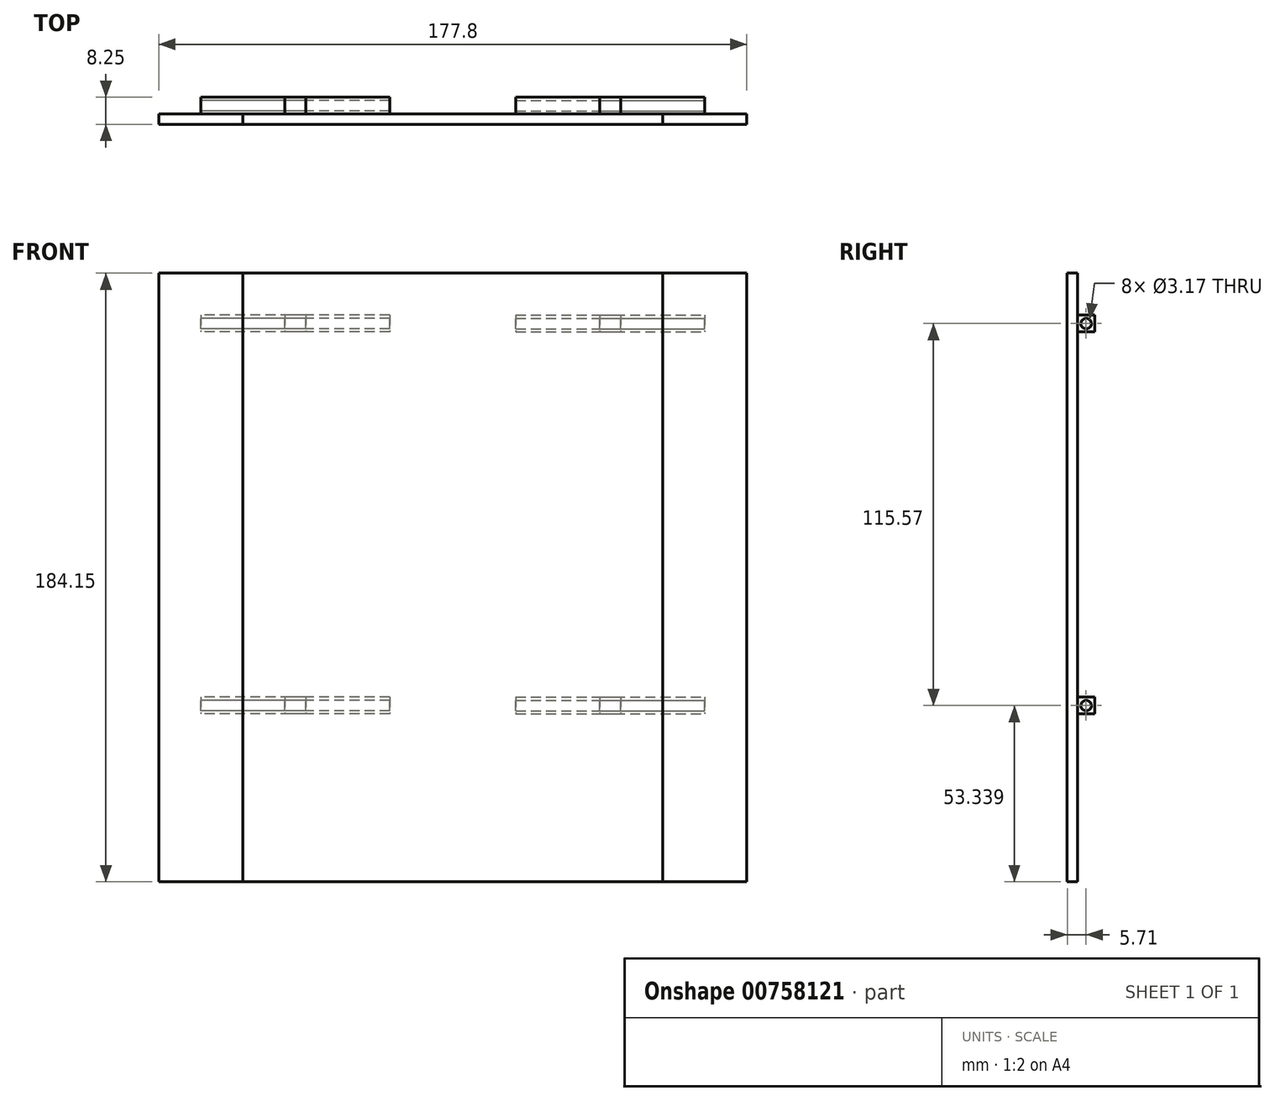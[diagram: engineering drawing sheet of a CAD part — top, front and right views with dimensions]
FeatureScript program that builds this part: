
annotation { "Feature Type Name" : "Feature", "Feature Type Description" : "" }
export const myFeature = defineFeature(function(context is Context, id is Id, definition is map)
    precondition{}
    {
        {
            var Q0;
            Q0=qCreatedBy(makeId("Front.planeOp"),FACE);
            var sketch = newSketch(context, id + "F0", { "sketchPlane" : qUnion([Q0])});
            skLineSegment(sketch, "E0", {"start": v(174.9, 31.47) * mm, "end": v(174.9, -152.68) * mm});
            skLineSegment(sketch, "E1", {"start": v(22.5, -152.68) * mm, "end": v(174.9, -152.68) * mm});
            skLineSegment(sketch, "E2", {"start": v(72.2, -149.5) * mm, "end": v(72.2, -81.5) * mm});
            skLineSegment(sketch, "E3", {"start": v(125.2, -81.5) * mm, "end": v(125.2, -149.5) * mm});
            skPoint(sketch, "E4.end.orphan", {"position": v(22.5, 4.94) * mm});
            skLineSegment(sketch, "E5", {"start": v(22.5, 31.47) * mm, "end": v(22.5, -152.68) * mm});
            skLineSegment(sketch, "E6", {"start": v(22.5, 31.47) * mm, "end": v(174.9, 31.47) * mm});
            skLineSegment(sketch, "E7", {"start": v(98.7, 31.47) * mm, "end": v(98.7, -152.68) * mm});
            skLineSegment(sketch, "E8", {"start": v(125.2, -81.5) * mm, "end": v(125.2, -81.5) * mm});
            skLineSegment(sketch, "E9", {"start": v(125.2, -81.5) * mm, "end": v(72.2, -81.5) * mm});
            skLineSegment(sketch, "E10", {"start": v(72.2, -81.5) * mm, "end": v(72.2, -81.5) * mm});
            skLineSegment(sketch, "E11", {"start": v(125.2, -149.5) * mm, "end": v(72.2, -149.5) * mm});
            skPoint(sketch, "E12", {"position": v(125.2, -149.5) * mm});
            skLineSegment(sketch, "E13.bottom", {"start": v(128.38, -78.33) * mm, "end": v(69.03, -78.33) * mm});
            skLineSegment(sketch, "E13.top", {"start": v(128.38, -152.68) * mm, "end": v(69.03, -152.68) * mm});
            skLineSegment(sketch, "E13.left", {"start": v(128.38, -78.33) * mm, "end": v(128.38, -152.68) * mm});
            skLineSegment(sketch, "E13.right", {"start": v(69.03, -78.33) * mm, "end": v(69.03, -152.68) * mm});
            skLineSegment(sketch, "E14", {"start": v(128.38, -115.5) * mm, "end": v(125.2, -115.5) * mm, "construction": true});
            skLineSegment(sketch, "E15", {"start": v(72.2, -115.5) * mm, "end": v(69.03, -115.5) * mm, "construction": true});
            skLineSegment(sketch, "E16", {"start": v(196.95, -166.3) * mm, "end": v(-6.25, -166.3) * mm, "construction": true});
            skLineSegment(sketch, "E17", {"start": v(-6.25, -166.3) * mm, "end": v(-6.25, 36.9) * mm, "construction": true});
            skLineSegment(sketch, "E18", {"start": v(-6.25, 36.9) * mm, "end": v(196.95, 36.9) * mm, "construction": true});
            skLineSegment(sketch, "E19", {"start": v(196.95, 36.9) * mm, "end": v(196.95, -166.3) * mm, "construction": true});
            skSolve(sketch);
        }
        {
            var Q0;
            {var subQ0=sQuery(id+"F0.wireOp",EDGE,"E3");Q0=makeQuery(id+"F0.imprint","IMPRINT",FACE,{"disambiguationData":[TD([[makeQuery(id+"F0.imprint","IMPRINT",EDGE,{"derivedFrom":subQ0}),1.0]])]});}
            var Q1;
            {var subQ3=sQuery(id+"F0.wireOp",EDGE,"ysnHI75o-22RJ-AJUc-xlc0-5ASTMfBeKelk");Q1=makeQuery(id+"F0.imprint","IMPRINT",FACE,{"disambiguationData":[TD([[makeQuery(id+"F0.imprint","IMPRINT",EDGE,{"derivedFrom":subQ3}),1.0]])]});}
            var Q2;
            {var subQ5=sQuery(id+"F0.wireOp",EDGE,"E0");Q2=makeQuery(id+"F0.imprint","IMPRINT",FACE,{"disambiguationData":[TD([[makeQuery(id+"F0.imprint","IMPRINT",EDGE,{"derivedFrom":subQ5}),-1.0]])]});}
            var Q3;
            {var subQ0=sQuery(id+"F0.wireOp",EDGE,"E3");Q3=makeQuery(id+"F0.imprint","IMPRINT",FACE,{"disambiguationData":[TD([[makeQuery(id+"F0.imprint","IMPRINT",EDGE,{"derivedFrom":subQ0}),-1.0]])]});}
            extrude(context, id + "F1", {"entities" : qUnion([Q0, Q1, Q2, Q3]), "depth" : 3.17 * mm, "offsetDistance" : 25.4 * mm});
        }
        {
            var Q0;
            Q0=makeQuery(id+"F1.opExtrude","SWEPT_FACE",FACE,{"disambiguationData":[OSD([sQuery(id+"F0.wireOp",EDGE,"E0")])]});
            var sketch = newSketch(context, id + "F2", { "sketchPlane" : qUnion([Q0])});
            skLineSegment(sketch, "E20.bottom", {"start": v(0, 18.77) * mm, "end": v(5.08, 18.77) * mm});
            skLineSegment(sketch, "E20.top", {"start": v(0, 13.69) * mm, "end": v(5.08, 13.69) * mm});
            skLineSegment(sketch, "E20.left", {"start": v(0, 18.77) * mm, "end": v(0, 13.69) * mm});
            skLineSegment(sketch, "E20.right", {"start": v(5.08, 18.77) * mm, "end": v(5.08, 13.69) * mm});
            skLineSegment(sketch, "E21.bottom", {"start": v(0, -96.8) * mm, "end": v(5.08, -96.8) * mm});
            skLineSegment(sketch, "E21.top", {"start": v(0, -101.88) * mm, "end": v(5.08, -101.88) * mm});
            skLineSegment(sketch, "E21.left", {"start": v(0, -96.8) * mm, "end": v(0, -101.88) * mm});
            skLineSegment(sketch, "E21.right", {"start": v(5.08, -96.8) * mm, "end": v(5.08, -101.88) * mm});
            skLineSegment(sketch, "E22", {"start": v(2.54, -101.88) * mm, "end": v(2.54, -96.8) * mm, "construction": true});
            skPoint(sketch, "E23", {"position": v(2.54, -99.34) * mm});
            skLineSegment(sketch, "E24", {"start": v(2.54, 18.77) * mm, "end": v(2.54, 13.69) * mm, "construction": true});
            skPoint(sketch, "E25", {"position": v(2.54, 16.23) * mm});
            skCircle(sketch, "E26", {"center": v(2.54, 16.23) * mm, "radius": 1.59 * mm});
            skCircle(sketch, "E27", {"center": v(2.54, -99.34) * mm, "radius": 1.59 * mm});
            skSolve(sketch);
        }
        {
            var Q0;
            Q0 = qSketchRegion(id + "F2", true);
            extrude(context, id + "F3", {"entities" : qUnion([Q0]), "operationType" : NewBodyOperationType.ADD, "oppositeDirection" : true, "depth" : 44.45 * mm, "offsetDistance" : 25.4 * mm, "hasSecondDirection" : true, "secondDirectionOppositeDirection" : true, "secondDirectionDepth" : 12.7 * mm});
        }
        {
            var Q0;
            Q0=makeQuery(id+"F1.opExtrude","SWEPT_BODY",BODY,{"disambiguationData":[OSD([sQuery(id+"F0.wireOp",EDGE,"E0"),sQuery(id+"F0.wireOp",EDGE,"E1"),sQuery(id+"F0.wireOp",EDGE,"E6"),sQuery(id+"F0.wireOp",EDGE,"E7"),sQuery(id+"F0.wireOp",EDGE,"E13.top")])]});
            var Q1;
            Q1=makeQuery(id+"F1.opExtrude","SWEPT_FACE",FACE,{"disambiguationData":[OSD([sQuery(id+"F0.wireOp",EDGE,"E7")])]});
            mirror(context, id + "F4", {"operationType" : NewBodyOperationType.ADD, "entities" : qUnion([Q0]), "mirrorPlane" : qUnion([Q1])});
        }
        {
            var Q0;
            Q0=makeQuery(id+"F2.imprint","IMPRINT",FACE,{"disambiguationData":[TD([[makeQuery(id+"F2.imprint","IMPRINT",EDGE,{"derivedFrom":sQuery(id+"F2.wireOp",EDGE,"E26")}),1.0]])]});
            var Q1;
            Q1=makeQuery(id+"F2.imprint","IMPRINT",FACE,{"disambiguationData":[TD([[makeQuery(id+"F2.imprint","IMPRINT",EDGE,{"derivedFrom":sQuery(id+"F2.wireOp",EDGE,"E27")}),1.0]])]});
            extrude(context, id + "F5", {"entities" : qUnion([Q0, Q1]), "oppositeDirection" : true, "depth" : 44.45 * mm, "offsetDistance" : 25.4 * mm, "hasSecondDirection" : true, "secondDirectionOppositeDirection" : false, "secondDirectionDepth" : 12.7 * mm});
        }
        {
            var Q0;
            Q0=makeQuery(id+"F4.opPattern","COPY",FACE,{"derivedFrom":makeQuery(id+"F3.opExtrude","CAP_FACE",FACE,{"disambiguationData":[OSD([sQuery(id+"F2.wireOp",EDGE,"E20.bottom"),sQuery(id+"F2.wireOp",EDGE,"E20.top"),sQuery(id+"F2.wireOp",EDGE,"E20.left"),sQuery(id+"F2.wireOp",EDGE,"E20.right"),sQuery(id+"F2.wireOp",EDGE,"E26")])],"isStart":false}),"instanceName":"1"});
            cPlane(context, id + "F6", {"entities" : qUnion([Q0]), "cplaneType" : CPlaneType.OFFSET, "offset" : 44.45 * mm, "width" : 152.4 * mm, "height" : 152.4 * mm});
        }
        {
            var Q0;
            Q0=makeQuery(id+"F1.opExtrude","SWEPT_BODY",BODY,{"disambiguationData":[OSD([sQuery(id+"F0.wireOp",EDGE,"E0"),sQuery(id+"F0.wireOp",EDGE,"E1"),sQuery(id+"F0.wireOp",EDGE,"E6"),sQuery(id+"F0.wireOp",EDGE,"E7")])]});
            var Q1;
            Q1=makeQuery(id+"F5.opExtrude","SWEPT_BODY",BODY,{"disambiguationData":[OSD([sQuery(id+"F2.wireOp",EDGE,"E26")])]});
            var Q2;
            Q2=makeQuery(id+"F5.opExtrude","SWEPT_BODY",BODY,{"disambiguationData":[OSD([sQuery(id+"F2.wireOp",EDGE,"E27")])]});
            var Q3;
            Q3=qCreatedBy(id+"F6.planeOp",FACE);
            mirror(context, id + "F7", {"entities" : qUnion([Q0, Q1, Q2]), "mirrorPlane" : qUnion([Q3])});
        }
    });
